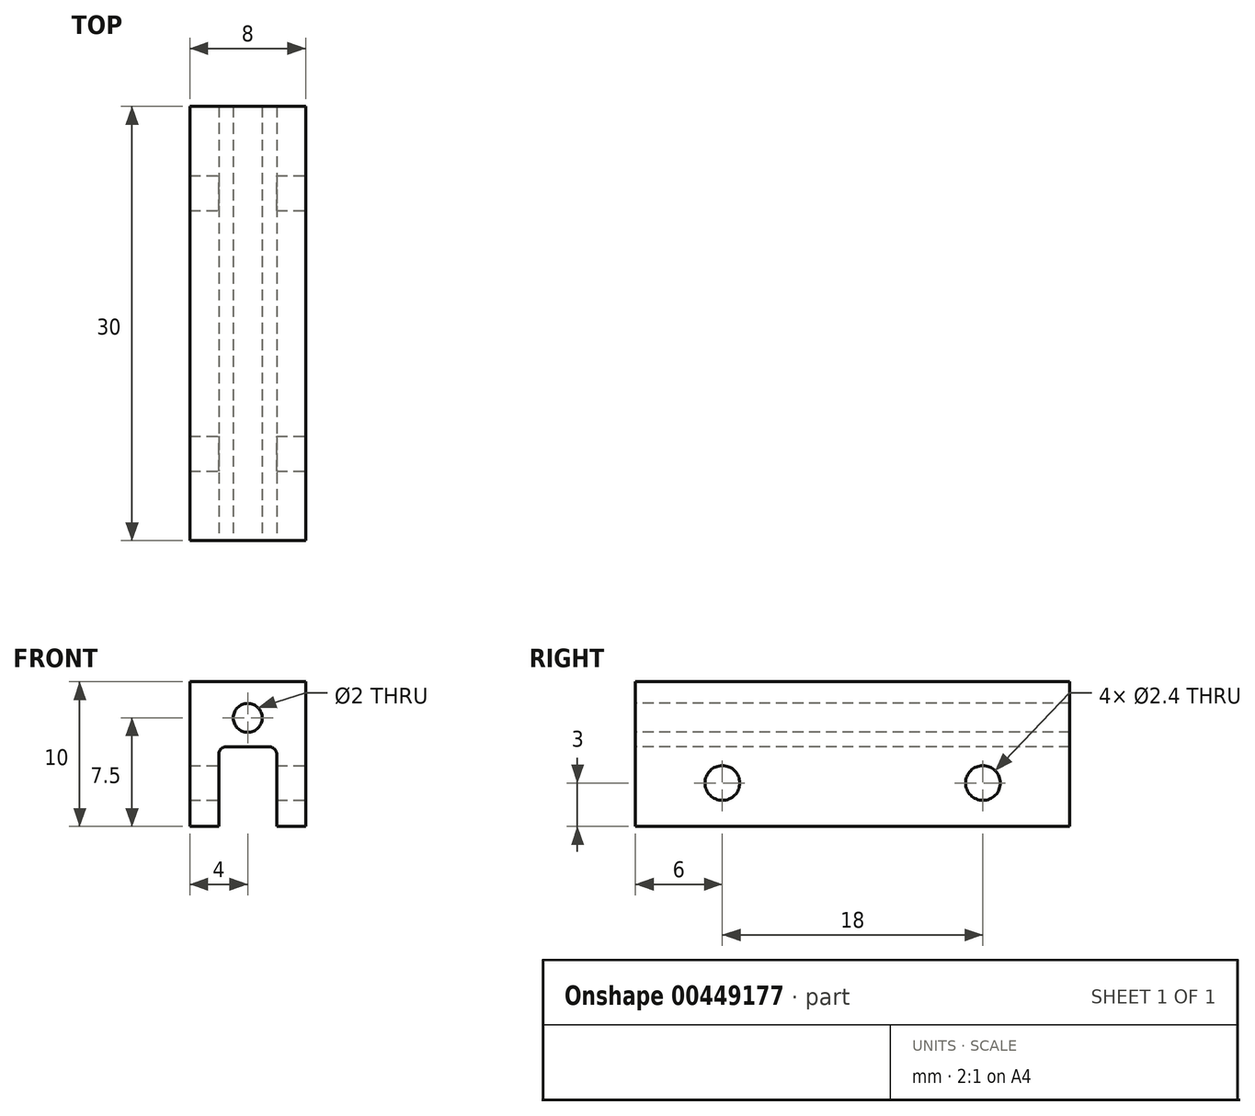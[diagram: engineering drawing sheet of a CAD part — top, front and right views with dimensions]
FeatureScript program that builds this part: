
annotation { "Feature Type Name" : "Feature", "Feature Type Description" : "" }
export const myFeature = defineFeature(function(context is Context, id is Id, definition is map)
    precondition{}
    {
        {
            var Q0;
            Q0=qCreatedBy(makeId("Front.planeOp"),FACE);
            var sketch = newSketch(context, id + "F0", { "sketchPlane" : qUnion([Q0])});
            skLineSegment(sketch, "E0.bottom", {"start": v(4, 5) * mm, "end": v(-4, 5) * mm});
            skLineSegment(sketch, "E0.top", {"start": v(4, -5) * mm, "end": v(-4, -5) * mm});
            skLineSegment(sketch, "E0.left", {"start": v(4, 5) * mm, "end": v(4, -5) * mm});
            skLineSegment(sketch, "E0.right", {"start": v(-4, 5) * mm, "end": v(-4, -5) * mm});
            skPoint(sketch, "E0.middle", {"position": v(0, 0) * mm});
            skSolve(sketch);
        }
        {
            var Q0;
            Q0 = qSketchRegion(id + "F0", true);
            extrude(context, id + "F1", {"entities" : qUnion([Q0]), "depth" : 15 * mm, "hasSecondDirection" : true, "secondDirectionOppositeDirection" : true, "secondDirectionDepth" : 15 * mm});
        }
        {
            var Q0;
            Q0=makeQuery(id+"F1.opExtrude","CAP_FACE",FACE,{"disambiguationData":[OSD([sQuery(id+"F0.wireOp",EDGE,"E0.bottom"),sQuery(id+"F0.wireOp",EDGE,"E0.top"),sQuery(id+"F0.wireOp",EDGE,"E0.left"),sQuery(id+"F0.wireOp",EDGE,"E0.right")])],"isStart":false});
            var sketch = newSketch(context, id + "F2", { "sketchPlane" : qUnion([Q0])});
            skCircle(sketch, "E1", {"center": v(0, 2.5) * mm, "radius": 1 * mm});
            skSolve(sketch);
        }
        {
            var Q0;
            Q0 = qSketchRegion(id + "F2", true);
            extrude(context, id + "F3", {"entities" : qUnion([Q0]), "operationType" : NewBodyOperationType.REMOVE, "endBound" : BoundingType.THROUGH_ALL, "oppositeDirection" : true, "depth" : 25 * mm});
        }
        {
            var Q0;
            Q0=makeQuery(id+"F1.opExtrude","CAP_FACE",FACE,{"disambiguationData":[OSD([sQuery(id+"F0.wireOp",EDGE,"E0.bottom"),sQuery(id+"F0.wireOp",EDGE,"E0.top"),sQuery(id+"F0.wireOp",EDGE,"E0.left"),sQuery(id+"F0.wireOp",EDGE,"E0.right")])],"isStart":false});
            var sketch = newSketch(context, id + "F4", { "sketchPlane" : qUnion([Q0])});
            skLineSegment(sketch, "E2.bottom", {"start": v(-2, -5) * mm, "end": v(2, -5) * mm});
            skLineSegment(sketch, "E2.top", {"start": v(-1.5, 0.5) * mm, "end": v(1.5, 0.5) * mm});
            skLineSegment(sketch, "E2.left", {"start": v(-2, -5) * mm, "end": v(-2, 0) * mm});
            skLineSegment(sketch, "E2.right", {"start": v(2, -5) * mm, "end": v(2, 0) * mm});
            skPoint(sketch, "E3.visualSharp", {"position": v(-2, 0.5) * mm});
            skArc(sketch, "E3.filletArc", {"start": v(-1.5, 0.5) * mm, "mid": v(-1.85, 0.35) * mm, "end": v(-2, 0) * mm});
            skPoint(sketch, "E4.visualSharp", {"position": v(2, 0.5) * mm});
            skArc(sketch, "E4.filletArc", {"start": v(2, 0) * mm, "mid": v(1.85, 0.35) * mm, "end": v(1.5, 0.5) * mm});
            skSolve(sketch);
        }
        {
            var Q0;
            Q0 = qSketchRegion(id + "F4", true);
            extrude(context, id + "F5", {"entities" : qUnion([Q0]), "operationType" : NewBodyOperationType.REMOVE, "endBound" : BoundingType.THROUGH_ALL, "oppositeDirection" : true, "depth" : 25 * mm});
        }
        {
            var Q0;
            Q0=makeQuery(id+"F1.opExtrude","SWEPT_FACE",FACE,{"disambiguationData":[OSD([sQuery(id+"F0.wireOp",EDGE,"E0.left")])]});
            var sketch = newSketch(context, id + "F6", { "sketchPlane" : qUnion([Q0])});
            skCircle(sketch, "E5", {"center": v(-9, -2) * mm, "radius": 1.2 * mm});
            skCircle(sketch, "E6", {"center": v(9, -2) * mm, "radius": 1.2 * mm});
            skSolve(sketch);
        }
        {
            var Q0;
            Q0 = qSketchRegion(id + "F6", true);
            extrude(context, id + "F7", {"entities" : qUnion([Q0]), "operationType" : NewBodyOperationType.REMOVE, "endBound" : BoundingType.THROUGH_ALL, "oppositeDirection" : true, "depth" : 25 * mm});
        }
    });
